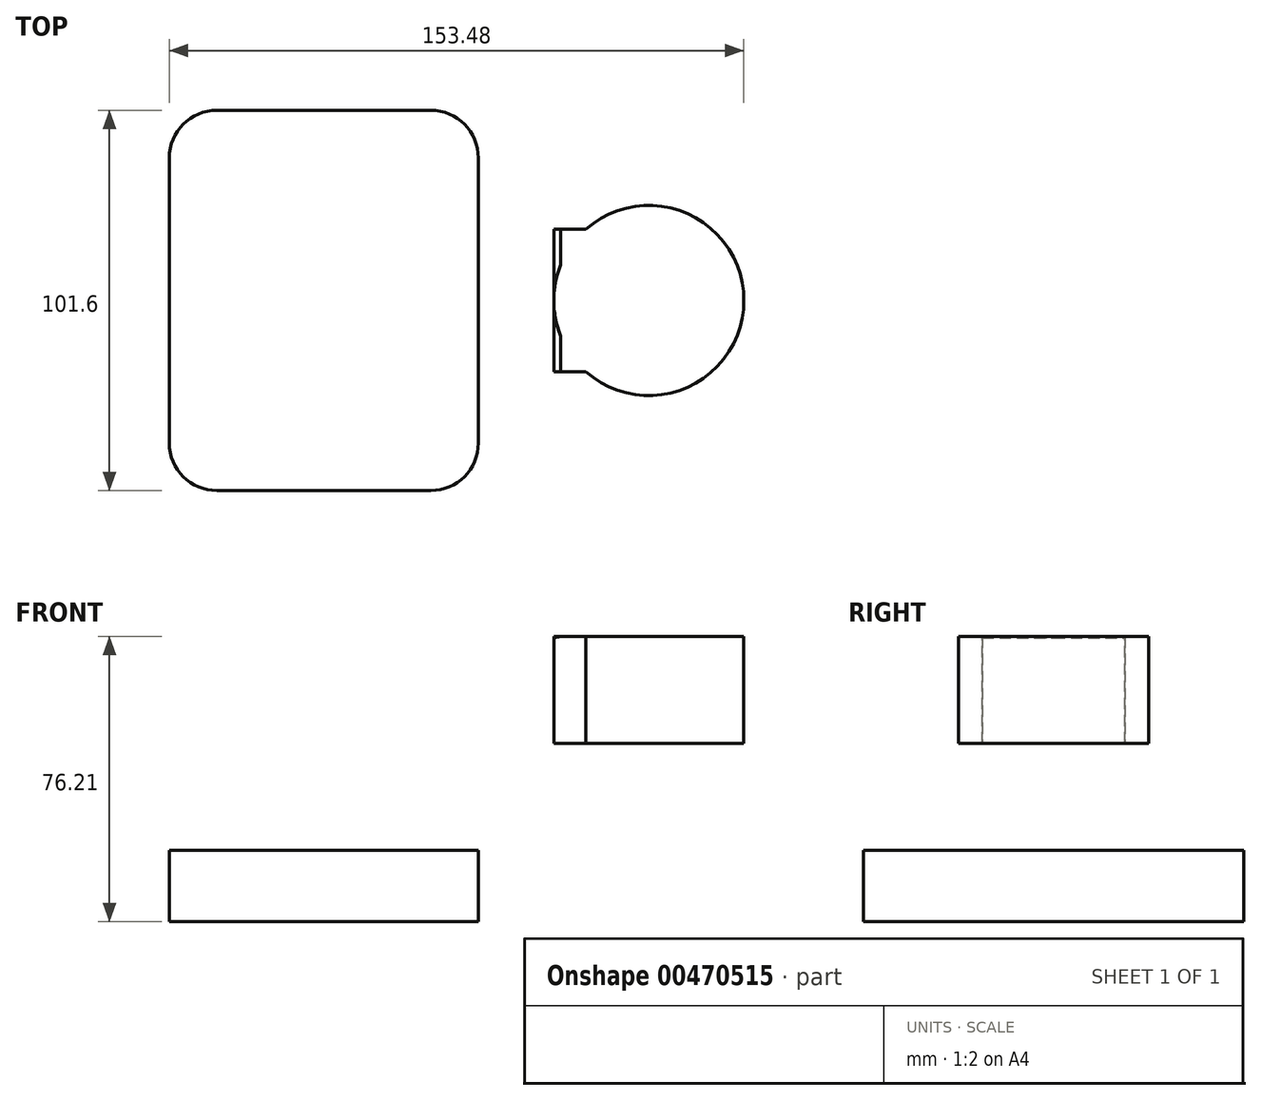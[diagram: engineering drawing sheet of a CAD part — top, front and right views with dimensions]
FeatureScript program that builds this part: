
annotation { "Feature Type Name" : "Feature", "Feature Type Description" : "" }
export const myFeature = defineFeature(function(context is Context, id is Id, definition is map)
    precondition{}
    {
        {
            var Q0;
            Q0=qCreatedBy(makeId("Front.planeOp"),FACE);
            var sketch = newSketch(context, id + "F0", { "sketchPlane" : qUnion([Q0])});
            skLineSegment(sketch, "E0.bottom", {"start": v(-41.28, -9.52) * mm, "end": v(41.28, -9.52) * mm});
            skLineSegment(sketch, "E0.top", {"start": v(-41.28, 9.53) * mm, "end": v(41.28, 9.53) * mm});
            skLineSegment(sketch, "E0.left", {"start": v(-41.28, -9.53) * mm, "end": v(-41.28, 9.53) * mm});
            skLineSegment(sketch, "E0.right", {"start": v(41.28, -9.53) * mm, "end": v(41.28, 9.53) * mm});
            skPoint(sketch, "E0.middle", {"position": v(0, 0) * mm});
            skLineSegment(sketch, "E1.bottom", {"start": v(112.21, 38.1) * mm, "end": v(61.41, 38.1) * mm});
            skLineSegment(sketch, "E1.top", {"start": v(112.21, 66.67) * mm, "end": v(61.41, 66.67) * mm});
            skLineSegment(sketch, "E1.left", {"start": v(112.21, 38.1) * mm, "end": v(112.21, 66.67) * mm});
            skLineSegment(sketch, "E1.right", {"start": v(61.41, 38.1) * mm, "end": v(61.41, 66.67) * mm});
            skPoint(sketch, "E1.middle", {"position": v(86.81, 52.39) * mm});
            skLineSegment(sketch, "E2", {"start": v(41.27, 9.53) * mm, "end": v(41.27, 41.5) * mm});
            skArc(sketch, "E3", {"start": v(41.27, 41.5) * mm, "mid": v(48.71, 59.47) * mm, "end": v(66.67, 66.9) * mm});
            skLineSegment(sketch, "E4", {"start": v(66.67, 66.9) * mm, "end": v(94.72, 66.9) * mm});
            skLineSegment(sketch, "E5.0", {"start": v(66.67, 85.96) * mm, "end": v(85.67, 85.96) * mm});
            skArc(sketch, "E5.1", {"start": v(22.22, 41.5) * mm, "mid": v(35.24, 72.94) * mm, "end": v(66.67, 85.96) * mm});
            skLineSegment(sketch, "E5.2", {"start": v(22.22, 5.72) * mm, "end": v(22.22, 41.5) * mm});
            skLineSegment(sketch, "E6", {"start": v(86.81, 38.1) * mm, "end": v(86.81, 85.96) * mm});
            skFitSpline(sketch, "E7", {"points": [v(-41.28, 9.52) * mm, v(66.67, 85.96) * mm], "startDerivative": vector(26.54, 116.79) * mm, "endDerivative": vector(174.7, 1.83) * mm});
            skSolve(sketch);
        }
        {
            var Q0;
            Q0=makeQuery(id+"F0.imprint","IMPRINT",FACE,{"disambiguationData":[TD([[makeQuery(id+"F0.imprint","IMPRINT",EDGE,{"derivedFrom":sQuery(id+"F0.wireOp",EDGE,"E0.bottom")}),1.0]])]});
            extrude(context, id + "F1", {"entities" : qUnion([Q0]), "endBound" : BoundingType.SYMMETRIC, "depth" : 101.6 * mm});
        }
        {
            var Q0;
            {var subQ1=sQuery(id+"F0.wireOp",EDGE,"E1.right");var subQ7=sQuery(id+"F0.wireOp",EDGE,"E1.bottom");var subQ9=makeQuery(id+"F0.imprint","INTERSECT",VERTEX,{"derivedFrom":[subQ7,subQ1]});Q0=makeQuery(id+"F0.imprint","IMPRINT",FACE,{"disambiguationData":[TD([[makeQuery(id+"F0.imprint","IMPRINT",EDGE,{"disambiguationData":[TD([[subQ9,1.0]])],"derivedFrom":subQ7}),-1.0]])]});}
            var Q1;
            {var subQ3=sQuery(id+"F0.wireOp",EDGE,"E5.2");var subQ5=sQuery(id+"F0.wireOp",EDGE,"E5.1");var subQ6=makeQuery(id+"F0.imprint","INTERSECT",VERTEX,{"derivedFrom":[subQ5,subQ3]});Q1=makeQuery(id+"F0.imprint","IMPRINT",FACE,{"disambiguationData":[TD([[makeQuery(id+"F0.imprint","IMPRINT",EDGE,{"disambiguationData":[TD([[subQ6,-1.0]])],"derivedFrom":subQ5}),1.0]])]});}
            extrude(context, id + "F2", {"entities" : qUnion([Q0, Q1]), "operationType" : NewBodyOperationType.ADD, "endBound" : BoundingType.SYMMETRIC, "depth" : 38.1 * mm});
        }
        {
            var Q0;
            {var subQ0=sQuery(id+"F0.wireOp",EDGE,"E1.left");Q0=makeQuery(id+"F0.imprint","IMPRINT",FACE,{"disambiguationData":[TD([[makeQuery(id+"F0.imprint","IMPRINT",EDGE,{"derivedFrom":subQ0}),1.0]])]});}
            var Q1;
            Q1=sQuery(id+"F0.wireOp",EDGE,"E6");
            revolve(context, id + "F3", {"operationType" : NewBodyOperationType.ADD, "entities" : qUnion([Q0]), "axis" : qUnion([Q1]), "revolveType" : RevolveType.FULL});
        }
        {
            var Q0;
            Q0=makeQuery(id+"F1.opExtrude","CAP_EDGE",EDGE,{"disambiguationData":[OSD([sQuery(id+"F0.wireOp",EDGE,"E0.left")])],"isStart":false});
            var Q1;
            Q1=makeQuery(id+"F1.opExtrude","CAP_EDGE",EDGE,{"disambiguationData":[OSD([sQuery(id+"F0.wireOp",EDGE,"E0.right")])],"isStart":false});
            var Q2;
            Q2=makeQuery(id+"F1.opExtrude","CAP_EDGE",EDGE,{"disambiguationData":[OSD([sQuery(id+"F0.wireOp",EDGE,"E0.right")])],"isStart":true});
            var Q3;
            Q3=makeQuery(id+"F1.opExtrude","CAP_EDGE",EDGE,{"disambiguationData":[OSD([sQuery(id+"F0.wireOp",EDGE,"E0.left")])],"isStart":true});
            fillet(context, id + "F4", {"entities" : qUnion([Q0, Q1, Q2, Q3]), "radius" : 12.7 * mm, "tangentPropagation" : true, "allowEdgeOverflow" : false});
        }
    });
